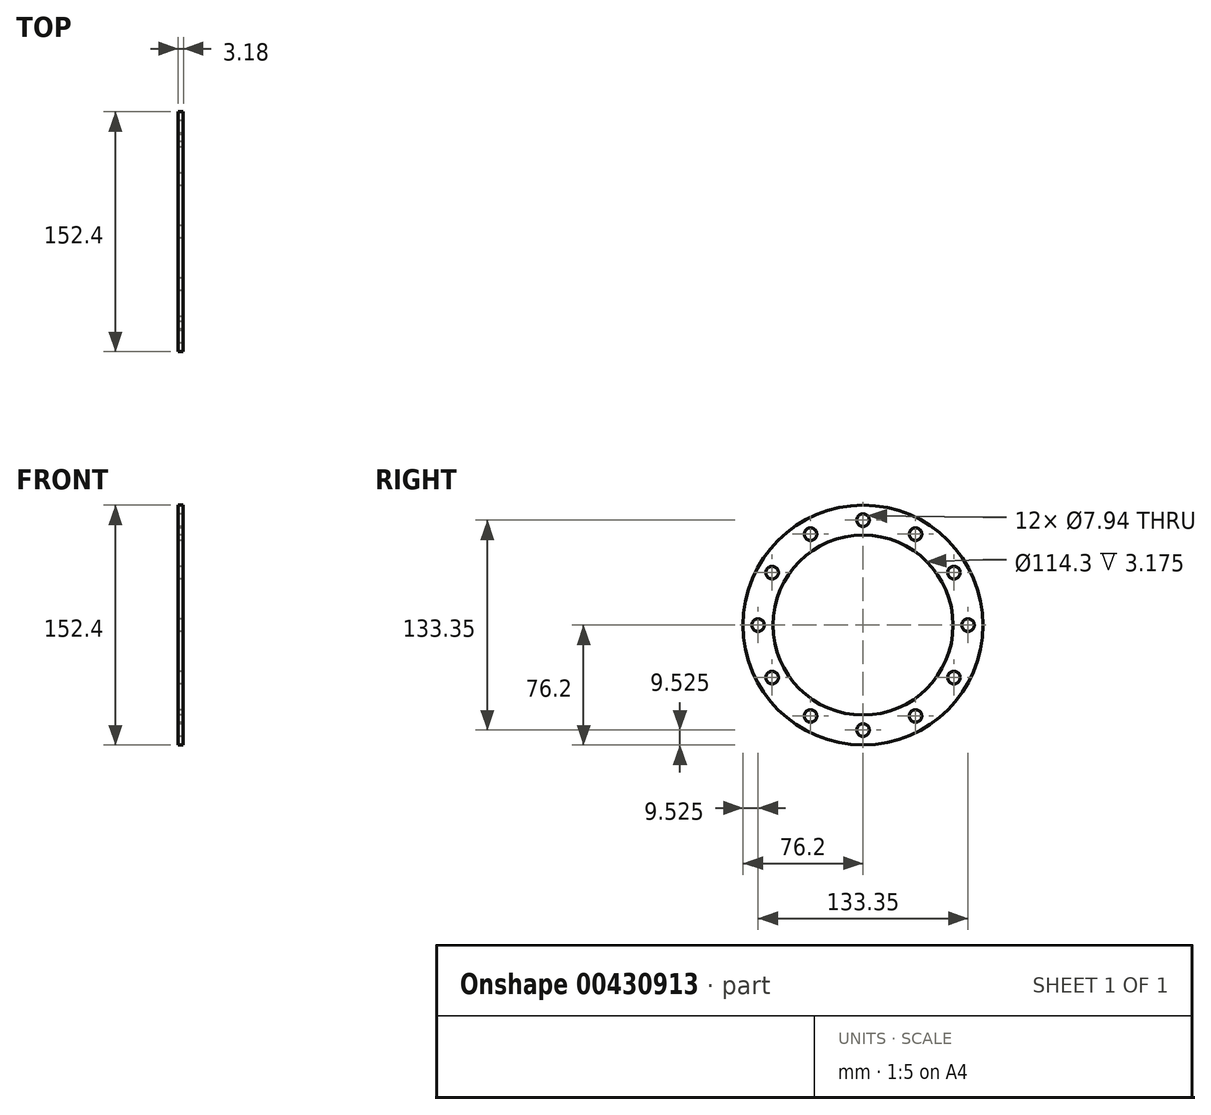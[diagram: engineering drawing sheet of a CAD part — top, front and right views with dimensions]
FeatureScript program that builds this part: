
annotation { "Feature Type Name" : "Feature", "Feature Type Description" : "" }
export const myFeature = defineFeature(function(context is Context, id is Id, definition is map)
    precondition{}
    {
        {
            var Q0;
            Q0=qCreatedBy(makeId("Right.planeOp"),FACE);
            var sketch = newSketch(context, id + "F0", { "sketchPlane" : qUnion([Q0])});
            skCircle(sketch, "E0", {"center": v(0, 0) * mm, "radius": 76.2 * mm});
            skCircle(sketch, "E1", {"center": v(0, 0) * mm, "radius": 57.15 * mm});
            skCircle(sketch, "E2", {"center": v(0, 66.68) * mm, "radius": 3.97 * mm});
            skCircle(sketch, "E3.1.0", {"center": v(-33.34, 57.74) * mm, "radius": 3.97 * mm});
            skCircle(sketch, "E3.2.0", {"center": v(-57.74, 33.34) * mm, "radius": 3.97 * mm});
            skCircle(sketch, "E3.3.0", {"center": v(-66.68, 0) * mm, "radius": 3.97 * mm});
            skCircle(sketch, "E3.4.0", {"center": v(-57.74, -33.34) * mm, "radius": 3.97 * mm});
            skCircle(sketch, "E3.5.0", {"center": v(-33.34, -57.74) * mm, "radius": 3.97 * mm});
            skCircle(sketch, "E3.6.0", {"center": v(0, -66.68) * mm, "radius": 3.97 * mm});
            skCircle(sketch, "E3.7.0", {"center": v(33.34, -57.74) * mm, "radius": 3.97 * mm});
            skCircle(sketch, "E3.8.0", {"center": v(57.74, -33.34) * mm, "radius": 3.97 * mm});
            skCircle(sketch, "E3.9.0", {"center": v(66.68, 0) * mm, "radius": 3.97 * mm});
            skCircle(sketch, "E3.10.0", {"center": v(57.74, 33.34) * mm, "radius": 3.97 * mm});
            skCircle(sketch, "E3.11.0", {"center": v(33.34, 57.74) * mm, "radius": 3.97 * mm});
            skSolve(sketch);
        }
        {
            var Q0;
            Q0=makeQuery(id+"F0.imprint","IMPRINT",FACE,{"disambiguationData":[TD([[makeQuery(id+"F0.imprint","IMPRINT",EDGE,{"derivedFrom":sQuery(id+"F0.wireOp",EDGE,"E0")}),1.0]])]});
            extrude(context, id + "F1", {"entities" : qUnion([Q0]), "depth" : 3.17 * mm});
        }
    });
